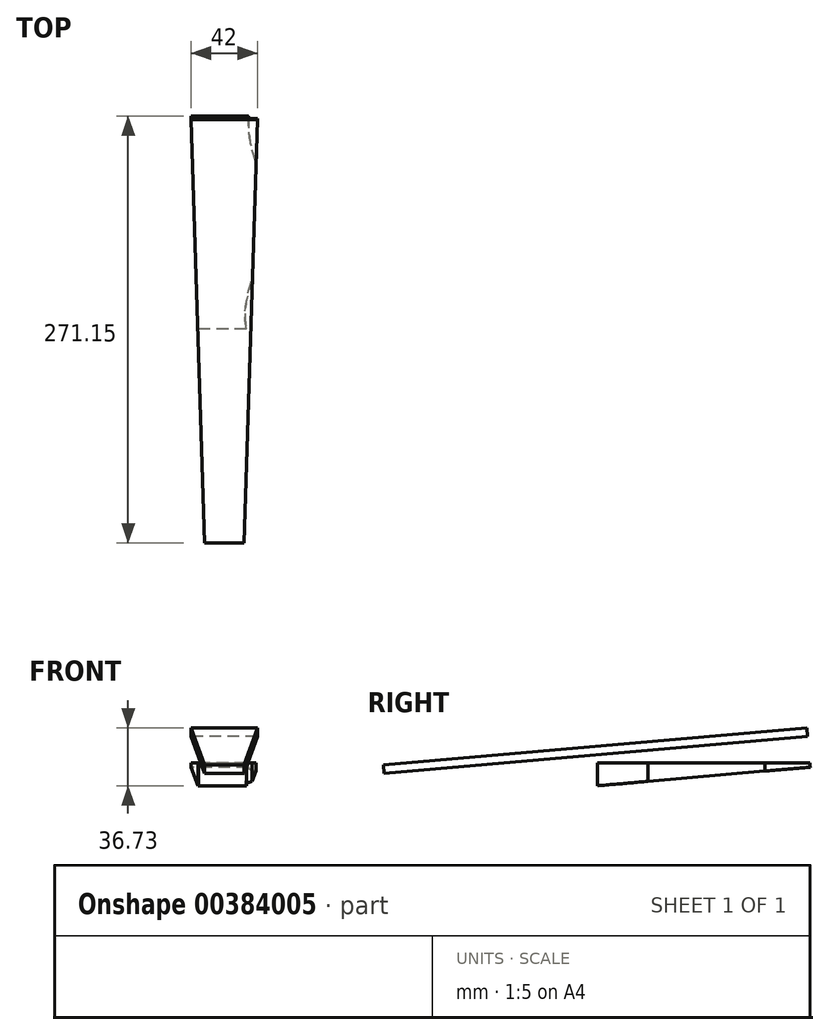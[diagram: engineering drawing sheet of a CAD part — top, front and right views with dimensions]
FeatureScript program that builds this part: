
annotation { "Feature Type Name" : "Feature", "Feature Type Description" : "" }
export const myFeature = defineFeature(function(context is Context, id is Id, definition is map)
    precondition{}
    {
        {
            var Q0;
            Q0=qCreatedBy(makeId("Right.planeOp"),FACE);
            var sketch = newSketch(context, id + "F0", { "sketchPlane" : qUnion([Q0])});
            skLineSegment(sketch, "E0", {"start": v(0, 0) * mm, "end": v(355.6, 0) * mm});
            skLineSegment(sketch, "E1", {"start": v(355.6, 0) * mm, "end": v(355.6, 34.92) * mm});
            skLineSegment(sketch, "E2", {"start": v(355.6, 34.92) * mm, "end": v(0, 34.92) * mm});
            skLineSegment(sketch, "E3", {"start": v(0, 34.92) * mm, "end": v(0, 0) * mm});
            skSolve(sketch);
        }
        {
            var Q0;
            Q0=qCreatedBy(makeId("Front.planeOp"),FACE);
            cPlane(context, id + "F1", {"entities" : qUnion([Q0]), "cplaneType" : CPlaneType.OFFSET, "offset" : 190 * mm, "oppositeDirection" : true, "width" : 152.4 * mm, "height" : 152.4 * mm});
        }
        {
            var Q0;
            Q0=qCreatedBy(id+"F1.planeOp",FACE);
            var sketch = newSketch(context, id + "F2", { "sketchPlane" : qUnion([Q0])});
            skLineSegment(sketch, "E4", {"start": v(20, 34.92) * mm, "end": v(-20, 34.92) * mm});
            skLineSegment(sketch, "E5", {"start": v(20, 34.92) * mm, "end": v(25, 63.14) * mm});
            skLineSegment(sketch, "E6", {"start": v(-20, 34.92) * mm, "end": v(-25, 63.14) * mm});
            skArc(sketch, "E7", {"start": v(25, 63.14) * mm, "mid": v(0, 67.92) * mm, "end": v(-25, 63.14) * mm});
            skSolve(sketch);
        }
        {
            var Q0;
            Q0=makeQuery(id+"F2.imprint","IMPRINT",FACE,{"disambiguationData":[TD([[makeQuery(id+"F2.imprint","IMPRINT",EDGE,{"derivedFrom":sQuery(id+"F2.wireOp",EDGE,"E4")}),-1.0]])]});
            extrude(context, id + "F3", {"entities" : qUnion([Q0]), "depth" : 5 * mm, "symmetric" : true});
        }
        {
            var Q0;
            Q0=makeQuery(id+"F0.imprint","IMPRINT",FACE,{"disambiguationData":[TD([[makeQuery(id+"F0.imprint","IMPRINT",EDGE,{"derivedFrom":sQuery(id+"F0.wireOp",EDGE,"E0")}),1.0]])]});
            extrude(context, id + "F4", {"entities" : qUnion([Q0]), "depth" : 203.2 * mm, "symmetric" : true});
        }
        {
            var Q0;
            Q0=qCreatedBy(makeId("Right.planeOp"),FACE);
            var sketch = newSketch(context, id + "F5", { "sketchPlane" : qUnion([Q0])});
            skLineSegment(sketch, "E8", {"start": v(0, 0) * mm, "end": v(-17.78, 0) * mm});
            skLineSegment(sketch, "E9", {"start": v(0, 0) * mm, "end": v(0, 40) * mm});
            skLineSegment(sketch, "E10", {"start": v(0, 40) * mm, "end": v(-135.48, 28.15) * mm});
            skLineSegment(sketch, "E11", {"start": v(-125.72, 16.25) * mm, "end": v(-36.34, 24.07) * mm});
            skArc(sketch, "E12", {"start": v(-17.78, 0) * mm, "mid": v(-20.48, 17.11) * mm, "end": v(-36.34, 24.07) * mm});
            skFitSpline(sketch, "E13", {"points": [v(-125.72, 16.25) * mm, v(-133.16, 9.44) * mm, v(-133.54, 0) * mm], "startDerivative": vector(-21.27, -3.72) * mm, "endDerivative": vector(5.45, -30.9) * mm});
            skFitSpline(sketch, "E14", {"points": [v(-133.54, 0) * mm, v(-157.94, 2.36) * mm, v(-195.17, -4.66) * mm, v(-233.81, -0.78) * mm, v(-234.79, 34.96) * mm, v(-207.08, 34.43) * mm, v(-211.87, 9.9) * mm], "startDerivative": vector(-104.85, 38.04) * mm, "endDerivative": vector(-196.55, -114) * mm});
            skLineSegment(sketch, "E15", {"start": v(-133.54, 0) * mm, "end": v(-133.54, 0) * mm});
            skLineSegment(sketch, "E16", {"start": v(-135.48, 28.15) * mm, "end": v(-141.46, 27.62) * mm});
            skFitSpline(sketch, "E17", {"points": [v(-141.46, 27.62) * mm, v(-170, 23.03) * mm, v(-195.1, 13.16) * mm, v(-211.87, 9.9) * mm], "startDerivative": vector(-79.33, -5.04) * mm, "endDerivative": vector(-57.4, 2.48) * mm});
            skSolve(sketch);
        }
        {
            var Q0;
            Q0 = qSketchRegion(id + "F5", true);
            extrude(context, id + "F6", {"entities" : qUnion([Q0]), "depth" : 25.4 * mm, "symmetric" : true});
        }
        {
            var Q0;
            Q0=makeQuery(id+"F4.opExtrude","SWEPT_FACE",FACE,{"disambiguationData":[OSD([sQuery(id+"F0.wireOp",EDGE,"E2")])]});
            var sketch = newSketch(context, id + "F7", { "sketchPlane" : qUnion([Q0])});
            skPoint(sketch, "E18.1.internal.snap0", {"position": v(0, 0) * mm});
            skLineSegment(sketch, "E19", {"start": v(54.42, 160.51) * mm, "end": v(-55.43, 160.51) * mm, "construction": true});
            skPoint(sketch, "E20", {"position": v(-0.5, 160.51) * mm});
            skLineSegment(sketch, "E21", {"start": v(14.08, 0) * mm, "end": v(-14.08, 0) * mm});
            skPoint(sketch, "E22.third.point", {"position": v(14.08, -234.32) * mm});
            skFitSpline(sketch, "E23", {"points": [v(14.08, 0) * mm, v(14.08, 17.5) * mm, v(50.28, 79.7) * mm], "startDerivative": vector(-9.66, 46.83) * mm, "endDerivative": vector(105.53, 72.25) * mm});
            skFitSpline(sketch, "E24", {"points": [v(-38.7, 350.24) * mm, v(33.57, 355.6) * mm], "startDerivative": vector(49.79, 21.68) * mm, "endDerivative": vector(100.72, 0) * mm});
            skFitSpline(sketch, "E25", {"points": [v(50.28, 79.7) * mm, v(16.81, 117.23) * mm, v(43.73, 249.62) * mm, v(101.6, 294.22) * mm], "startDerivative": vector(-190.85, 79.76) * mm, "endDerivative": vector(311.15, 35.93) * mm});
            skFitSpline(sketch, "E26", {"points": [v(33.57, 355.6) * mm, v(101.6, 294.22) * mm], "startDerivative": vector(148.25, 0) * mm, "endDerivative": vector(0, -88.63) * mm});
            skFitSpline(sketch, "E27", {"points": [v(-74.52, 129.23) * mm, v(-55.49, 143.24) * mm, v(-63.42, 175.84) * mm], "startDerivative": vector(101.46, -11.79) * mm, "endDerivative": vector(-13.25, 108.63) * mm});
            skFitSpline(sketch, "E28", {"points": [v(-63.42, 175.84) * mm, v(-30.81, 175.84) * mm, v(-19.95, 215.73) * mm, v(-38.7, 350.24) * mm], "startDerivative": vector(122.3, -20.72) * mm, "endDerivative": vector(-55.08, 184.05) * mm});
            skLineSegment(sketch, "E29", {"start": v(-74.52, 129.23) * mm, "end": v(-78.33, 125.57) * mm});
            skFitSpline(sketch, "E30", {"points": [v(-78.33, 125.57) * mm, v(-72.25, 107.7) * mm, v(-78.33, 83.22) * mm], "startDerivative": vector(27.4, -35.65) * mm, "endDerivative": vector(-13.48, -31.73) * mm});
            skFitSpline(sketch, "E31", {"points": [v(-14.08, 0) * mm, v(-56.33, 12.8) * mm, v(-78.33, 83.22) * mm], "startDerivative": vector(-99.84, -1.47) * mm, "endDerivative": vector(49.74, 195.74) * mm});
            skSolve(sketch);
        }
        {
            var Q0;
            Q0 = qSketchRegion(id + "F7", true);
            extrude(context, id + "F8", {"entities" : qUnion([Q0]), "operationType" : NewBodyOperationType.INTERSECT, "oppositeDirection" : true, "depth" : 127 * mm, "symmetric" : true});
        }
        {
            var Q0;
            Q0=qCreatedBy(makeId("Right.planeOp"),FACE);
            var sketch = newSketch(context, id + "F9", { "sketchPlane" : qUnion([Q0])});
            skLineSegment(sketch, "E32", {"start": v(10.31, 0) * mm, "end": v(321.83, 0) * mm});
            skFitSpline(sketch, "E33", {"points": [v(10.31, 0) * mm, v(33.84, 17.14) * mm, v(127.85, 21.54) * mm, v(172.28, 9.76) * mm], "startDerivative": vector(35.1, 64.3) * mm, "endDerivative": vector(135.5, -80.78) * mm});
            skFitSpline(sketch, "E34", {"points": [v(172.28, 9.76) * mm, v(220.22, 15.57) * mm, v(264.42, 11.56) * mm, v(321.83, 0) * mm], "startDerivative": vector(175, 55.94) * mm, "endDerivative": vector(236.83, -12.13) * mm});
            skLineSegment(sketch, "E35", {"start": v(86.07, 23.25) * mm, "end": v(86.07, 34.92) * mm, "construction": true});
            skSolve(sketch);
        }
        {
            var Q0;
            Q0 = qSketchRegion(id + "F9", true);
            extrude(context, id + "F10", {"entities" : qUnion([Q0]), "operationType" : NewBodyOperationType.REMOVE, "oppositeDirection" : true, "depth" : 177.8 * mm, "symmetric" : true});
        }
        {
            var Q0;
            Q0=makeQuery(id+"F4.opExtrude","SWEPT_FACE",FACE,{"disambiguationData":[OSD([sQuery(id+"F0.wireOp",EDGE,"E2")])]});
            var sketch = newSketch(context, id + "F11", { "sketchPlane" : qUnion([Q0])});
            skCircle(sketch, "E36", {"center": v(-70.24, 59.76) * mm, "radius": 30 * mm});
            skSolve(sketch);
        }
        {
            var Q0;
            Q0 = qSketchRegion(id + "F11", true);
            extrude(context, id + "F12", {"entities" : qUnion([Q0]), "operationType" : NewBodyOperationType.REMOVE, "endBound" : BoundingType.THROUGH_ALL, "oppositeDirection" : true, "depth" : 25 * mm});
        }
        {
            var Q0;
            Q0=qCreatedBy(makeId("Right.planeOp"),FACE);
            var sketch = newSketch(context, id + "F13", { "sketchPlane" : qUnion([Q0])});
            skLineSegment(sketch, "E37", {"start": v(-141.46, 27.62) * mm, "end": v(-141, 33.89) * mm});
            skLineSegment(sketch, "E38", {"start": v(-141, 33.89) * mm, "end": v(-136.02, 34.32) * mm});
            skLineSegment(sketch, "E39", {"start": v(-136.02, 34.32) * mm, "end": v(-135.48, 28.15) * mm});
            skLineSegment(sketch, "E40", {"start": v(-135.48, 28.15) * mm, "end": v(-141.46, 27.62) * mm});
            skSolve(sketch);
        }
        {
            var Q0;
            Q0 = qSketchRegion(id + "F13", true);
            extrude(context, id + "F14", {"entities" : qUnion([Q0]), "depth" : 25 * mm, "symmetric" : true});
        }
        {
            var Q0;
            Q0=qCreatedBy(makeId("Right.planeOp"),FACE);
            var sketch = newSketch(context, id + "F15", { "sketchPlane" : qUnion([Q0])});
            skLineSegment(sketch, "E41.bottom", {"start": v(-135.48, 28.15) * mm, "end": v(133.5, 51.68) * mm});
            skLineSegment(sketch, "E41.top", {"start": v(-135.96, 33.63) * mm, "end": v(133.01, 57.16) * mm});
            skLineSegment(sketch, "E41.left", {"start": v(-135.48, 28.15) * mm, "end": v(-135.96, 33.63) * mm});
            skLineSegment(sketch, "E41.right", {"start": v(133.5, 51.68) * mm, "end": v(133.01, 57.16) * mm});
            skLineSegment(sketch, "E42", {"start": v(133.01, 57.16) * mm, "end": v(133.01, 34.92) * mm, "construction": true});
            skSolve(sketch);
        }
        {
            var Q0;
            Q0 = qSketchRegion(id + "F15", true);
            extrude(context, id + "F16", {"entities" : qUnion([Q0]), "depth" : 42 * mm, "symmetric" : true});
        }
        {
            var Q0;
            Q0=makeQuery(id+"F16.opExtrude","SWEPT_FACE",FACE,{"disambiguationData":[OSD([sQuery(id+"F15.wireOp",EDGE,"E41.top")])]});
            var sketch = newSketch(context, id + "F17", { "sketchPlane" : qUnion([Q0])});
            skLineSegment(sketch, "E43", {"start": v(-21, 137.49) * mm, "end": v(21, 137.49) * mm});
            skLineSegment(sketch, "E44", {"start": v(21, 137.49) * mm, "end": v(12.5, -132.51) * mm});
            skLineSegment(sketch, "E45", {"start": v(12.5, -132.51) * mm, "end": v(-12.5, -132.51) * mm});
            skLineSegment(sketch, "E46", {"start": v(-12.5, -132.51) * mm, "end": v(-21, 137.49) * mm});
            skLineSegment(sketch, "E47", {"start": v(-16.75, 2.49) * mm, "end": v(16.75, 2.49) * mm, "construction": true});
            skSolve(sketch);
        }
        {
            var Q0;
            Q0=makeQuery(id+"F17.imprint","IMPRINT",FACE,{"disambiguationData":[TD([[makeQuery(id+"F17.imprint","IMPRINT",EDGE,{"derivedFrom":sQuery(id+"F17.wireOp",EDGE,"E43")}),1.0]])]});
            extrude(context, id + "F18", {"entities" : qUnion([Q0]), "operationType" : NewBodyOperationType.INTERSECT, "oppositeDirection" : true, "depth" : 25 * mm});
        }
    });
